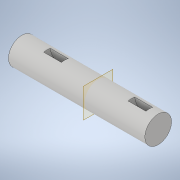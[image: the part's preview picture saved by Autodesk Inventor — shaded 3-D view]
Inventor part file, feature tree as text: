
AUTODESK INVENTOR PART (.ipt)
format: ipt  version: 2021 (Build 250183000, 183)  size: 118,272 bytes
history: native  units: in
note: dims shown in document units (in); Inventor stores cm internally (conversion verified against a paired STEP export)
features: extrude x3, sketch x3, plane x1, mirror x1
ambient origin geometry x8: Origin, YZ Plane, XZ Plane, XY Plane, X Axis, Y Axis, Z Axis, Center Point
bodies: Solid1 (feature_tree)
feature tree (8):
  extrude  "Extrusion1"  Depth=3.375in TaperAngle=0.0deg
  extrude  "Extrusion3"  Depth=0.5in
  plane  "Work Plane1"
  mirror  "Mirror1"
  extrude  "Extrusion5"  [1 undecoded]
  sketch  "Sketch1"  dims[d0=0.75in d1=3.375in d2=0.0in]
  sketch  "Sketch3"  dims[d7=0.5in d8=0.5in]
  sketch  "Sketch5"  dims[d9=0.188in d10=0.0in d11=-1.6878in d14=0.459in d15=0.0in]
note: 1 required parameter value undecoded (feature->parameter linkage not recoverable at this tier; creation-order binding heuristic only, values carry confidence <= 0.55)
